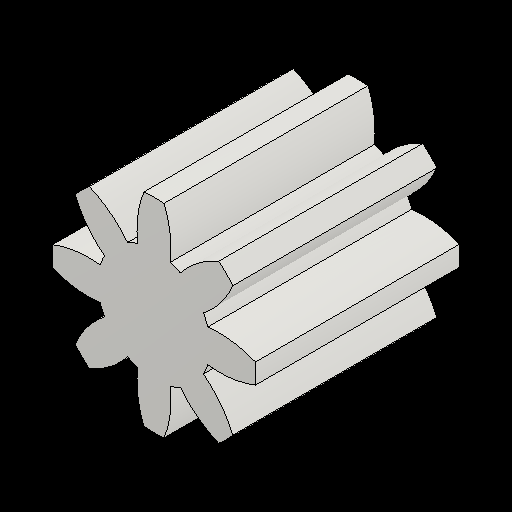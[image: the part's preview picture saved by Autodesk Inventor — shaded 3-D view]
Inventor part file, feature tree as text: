
AUTODESK INVENTOR PART (.ipt)
format: ipt  version: 2023.2 (Build 272271030, 271C)  size: 177,152 bytes
history: native  units: mm (DEFAULTED — no unit token found)
features: plane x3, other x3, sketch x2, extrude x1
ambient origin geometry x8: Origin, YZ Plane, XZ Plane, XY Plane, X Axis, Y Axis, Z Axis, Center Point
bodies: Solid1 (feature_tree)
feature tree (9):
  extrude  "Extrusion1"  Depth=10.0mm TaperAngle=0.0deg
  plane  "Work Plane2"
  plane  "Work Plane8"
  plane  "Work Plane9"
  other  "Spur Gear"
  sketch  "Sketch1"  dims[d0=10.0mm d1=10.0mm d2=0.0mm]
  sketch  "Sketch2"  dims[d3=8.0mm d4=10.0mm d5=0.0mm d16=14.0mm d17=0.0mm d34=22.5deg d39=0.0mm d41=0.0mm d43=14.0mm d46=14.0mm d47=0.0mm d48=0.0mm]
  other  "Srf1"
  other  "Pitch Diameter"
